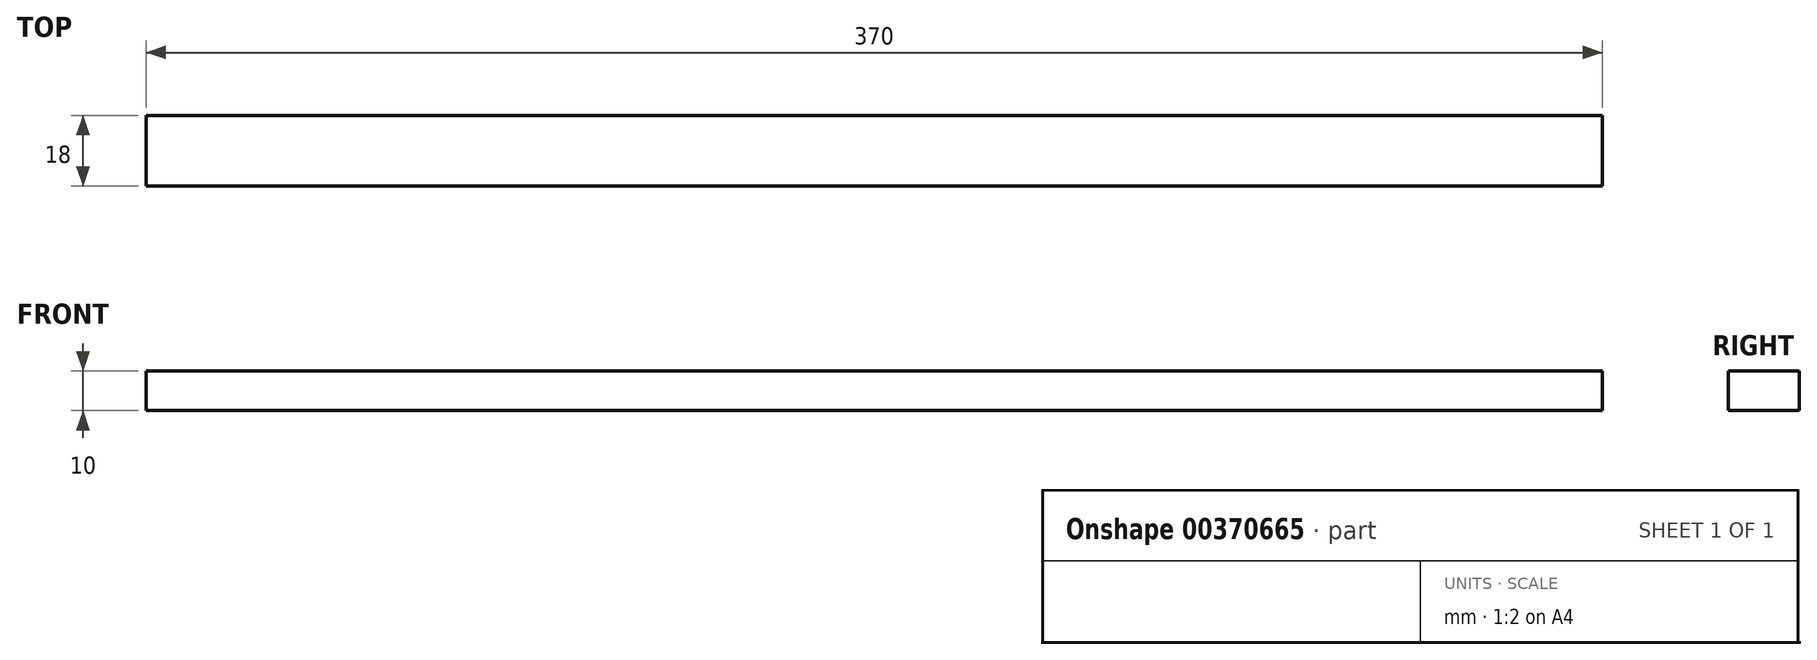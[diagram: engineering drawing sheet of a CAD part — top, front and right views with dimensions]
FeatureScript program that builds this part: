
annotation { "Feature Type Name" : "Feature", "Feature Type Description" : "" }
export const myFeature = defineFeature(function(context is Context, id is Id, definition is map)
    precondition{}
    {
        {
            var Q0;
            Q0=qCreatedBy(makeId("Front.planeOp"),FACE);
            var sketch = newSketch(context, id + "F0", { "sketchPlane" : qUnion([Q0])});
            skLineSegment(sketch, "E0.bottom", {"start": v(-185, 0) * mm, "end": v(185, 0) * mm});
            skLineSegment(sketch, "E0.top", {"start": v(-185, -10) * mm, "end": v(185, -10) * mm});
            skLineSegment(sketch, "E0.left", {"start": v(-185, 0) * mm, "end": v(-185, -10) * mm});
            skLineSegment(sketch, "E0.right", {"start": v(185, 0) * mm, "end": v(185, -10) * mm});
            skSolve(sketch);
        }
        {
            var Q0;
            Q0 = qSketchRegion(id + "F0", true);
            extrude(context, id + "F1", {"entities" : qUnion([Q0]), "depth" : 18 * mm});
        }
    });
